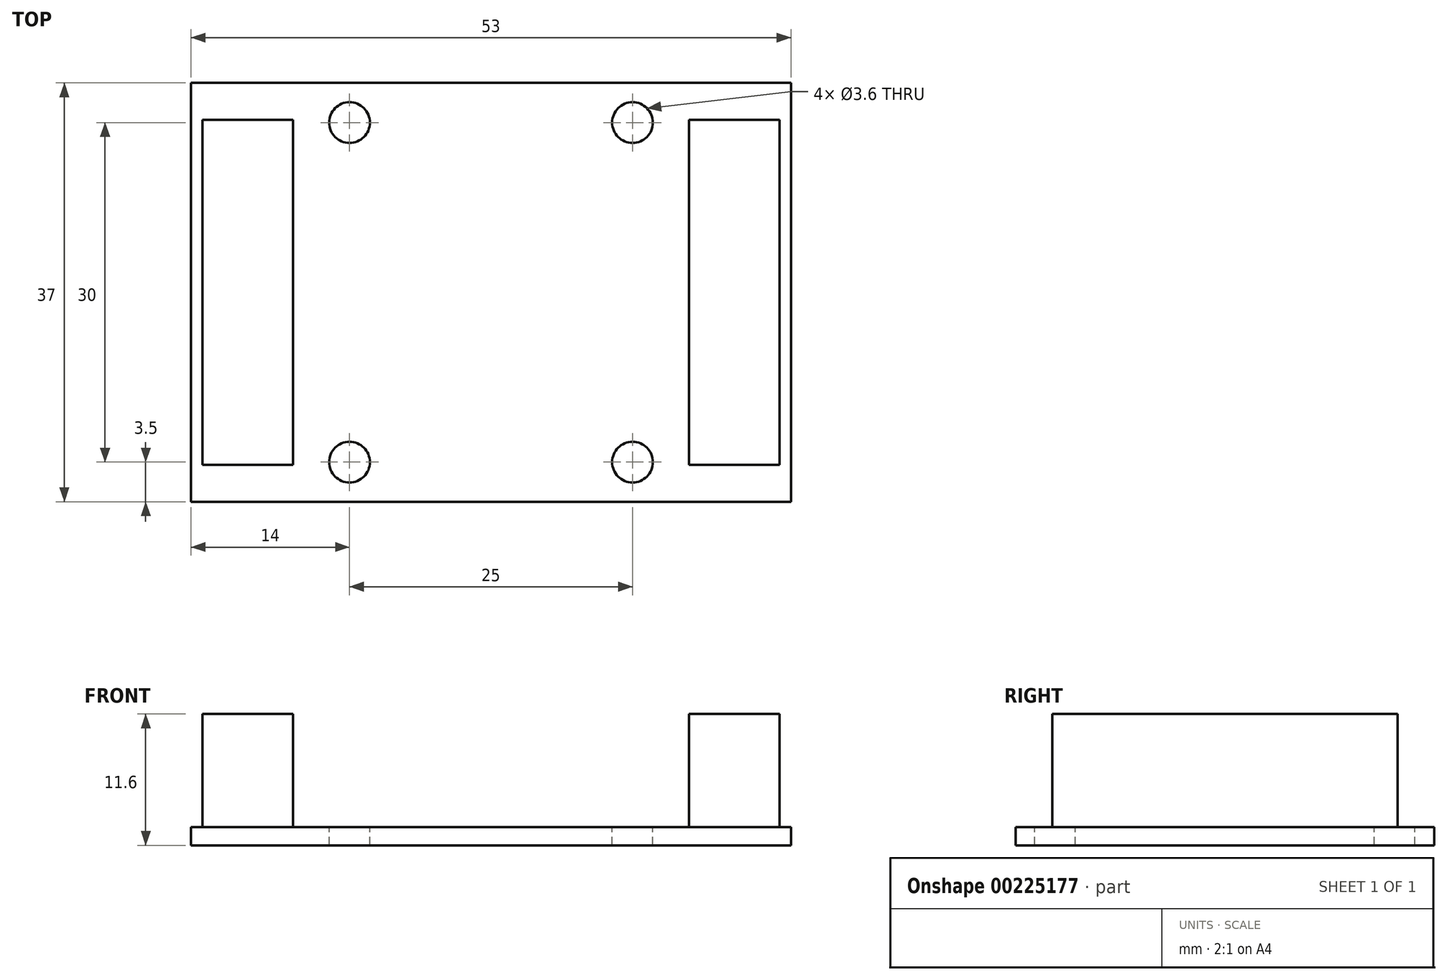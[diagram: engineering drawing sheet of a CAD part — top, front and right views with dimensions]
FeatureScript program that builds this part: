
annotation { "Feature Type Name" : "Feature", "Feature Type Description" : "" }
export const myFeature = defineFeature(function(context is Context, id is Id, definition is map)
    precondition{}
    {
        {
            var Q0;
            Q0=qCreatedBy(makeId("Top.planeOp"),FACE);
            var sketch = newSketch(context, id + "F0", { "sketchPlane" : qUnion([Q0])});
            skLineSegment(sketch, "E0.bottom", {"start": v(26.5, -18.5) * mm, "end": v(-26.5, -18.5) * mm});
            skLineSegment(sketch, "E0.top", {"start": v(26.5, 18.5) * mm, "end": v(-26.5, 18.5) * mm});
            skLineSegment(sketch, "E0.left", {"start": v(26.5, -18.5) * mm, "end": v(26.5, 18.5) * mm});
            skLineSegment(sketch, "E0.right", {"start": v(-26.5, -18.5) * mm, "end": v(-26.5, 18.5) * mm});
            skPoint(sketch, "E0.middle", {"position": v(0, 0) * mm});
            skSolve(sketch);
        }
        {
            var Q0;
            Q0=makeQuery(id+"F0.imprint","IMPRINT",FACE,{"disambiguationData":[TD([[makeQuery(id+"F0.imprint","IMPRINT",EDGE,{"derivedFrom":sQuery(id+"F0.wireOp",EDGE,"E0.bottom")}),-1.0]])]});
            extrude(context, id + "F1", {"entities" : qUnion([Q0]), "depth" : 1.6 * mm});
        }
        {
            var Q0;
            Q0=makeQuery(id+"F1.opExtrude","CAP_FACE",FACE,{"disambiguationData":[OSD([sQuery(id+"F0.wireOp",EDGE,"E0.bottom"),sQuery(id+"F0.wireOp",EDGE,"E0.top"),sQuery(id+"F0.wireOp",EDGE,"E0.left"),sQuery(id+"F0.wireOp",EDGE,"E0.right")])],"isStart":false});
            var sketch = newSketch(context, id + "F2", { "sketchPlane" : qUnion([Q0])});
            skLineSegment(sketch, "E1.bottom", {"start": v(-25.5, 15.25) * mm, "end": v(-17.5, 15.25) * mm});
            skLineSegment(sketch, "E1.top", {"start": v(-25.5, -15.25) * mm, "end": v(-17.5, -15.25) * mm});
            skLineSegment(sketch, "E1.left", {"start": v(-25.5, 15.25) * mm, "end": v(-25.5, -15.25) * mm});
            skLineSegment(sketch, "E1.right", {"start": v(-17.5, 15.25) * mm, "end": v(-17.5, -15.25) * mm});
            skLineSegment(sketch, "E2.bottom", {"start": v(17.5, 15.25) * mm, "end": v(25.5, 15.25) * mm});
            skLineSegment(sketch, "E2.top", {"start": v(17.5, -15.25) * mm, "end": v(25.5, -15.25) * mm});
            skLineSegment(sketch, "E2.left", {"start": v(17.5, 15.25) * mm, "end": v(17.5, -15.25) * mm});
            skLineSegment(sketch, "E2.right", {"start": v(25.5, 15.25) * mm, "end": v(25.5, -15.25) * mm});
            skSolve(sketch);
        }
        {
            var Q0;
            Q0=makeQuery(id+"F2.imprint","IMPRINT",FACE,{"disambiguationData":[TD([[makeQuery(id+"F2.imprint","IMPRINT",EDGE,{"derivedFrom":sQuery(id+"F2.wireOp",EDGE,"E2.bottom")}),-1.0]])]});
            var Q1;
            Q1=makeQuery(id+"F2.imprint","IMPRINT",FACE,{"disambiguationData":[TD([[makeQuery(id+"F2.imprint","IMPRINT",EDGE,{"derivedFrom":sQuery(id+"F2.wireOp",EDGE,"E1.bottom")}),-1.0]])]});
            extrude(context, id + "F3", {"entities" : qUnion([Q0, Q1]), "operationType" : NewBodyOperationType.ADD, "depth" : 10 * mm});
        }
        {
            var Q0;
            Q0=makeQuery(id+"F1.opExtrude","CAP_FACE",FACE,{"disambiguationData":[OSD([sQuery(id+"F0.wireOp",EDGE,"E0.bottom"),sQuery(id+"F0.wireOp",EDGE,"E0.top"),sQuery(id+"F0.wireOp",EDGE,"E0.left"),sQuery(id+"F0.wireOp",EDGE,"E0.right")])],"isStart":false});
            var sketch = newSketch(context, id + "F4", { "sketchPlane" : qUnion([Q0])});
            skCircle(sketch, "E3", {"center": v(12.5, -15) * mm, "radius": 1.8 * mm});
            skCircle(sketch, "E4.0.1.0", {"center": v(12.5, 15) * mm, "radius": 1.8 * mm});
            skCircle(sketch, "E4.1.0.0", {"center": v(-12.5, -15) * mm, "radius": 1.8 * mm});
            skCircle(sketch, "E4.1.1.0", {"center": v(-12.5, 15) * mm, "radius": 1.8 * mm});
            skLineSegment(sketch, "E4.direction1", {"start": v(12.5, -15) * mm, "end": v(-12.5, -15) * mm, "construction": true});
            skLineSegment(sketch, "E4.direction2", {"start": v(12.5, -15) * mm, "end": v(12.5, 15) * mm, "construction": true});
            skSolve(sketch);
        }
        {
            var Q0;
            Q0=makeQuery(id+"F4.imprint","IMPRINT",FACE,{"disambiguationData":[TD([[makeQuery(id+"F4.imprint","IMPRINT",EDGE,{"derivedFrom":sQuery(id+"F4.wireOp",EDGE,"E3")}),1.0]])]});
            var Q1;
            Q1=makeQuery(id+"F4.imprint","IMPRINT",FACE,{"disambiguationData":[TD([[makeQuery(id+"F4.imprint","IMPRINT",EDGE,{"derivedFrom":sQuery(id+"F4.wireOp",EDGE,"E4.0.1.0")}),1.0]])]});
            var Q2;
            Q2=makeQuery(id+"F4.imprint","IMPRINT",FACE,{"disambiguationData":[TD([[makeQuery(id+"F4.imprint","IMPRINT",EDGE,{"derivedFrom":sQuery(id+"F4.wireOp",EDGE,"E4.1.1.0")}),1.0]])]});
            var Q3;
            Q3=makeQuery(id+"F4.imprint","IMPRINT",FACE,{"disambiguationData":[TD([[makeQuery(id+"F4.imprint","IMPRINT",EDGE,{"derivedFrom":sQuery(id+"F4.wireOp",EDGE,"E4.1.0.0")}),1.0]])]});
            var Q4;
            Q4=sQuery(id+"F4.wireOp",EDGE,"E3");
            var Q5;
            Q5=sQuery(id+"F4.wireOp",EDGE,"E4.0.1.0");
            var Q6;
            Q6=sQuery(id+"F4.wireOp",EDGE,"E4.1.1.0");
            var Q7;
            Q7=sQuery(id+"F4.wireOp",EDGE,"E4.1.0.0");
            extrude(context, id + "F5", {"entities" : qUnion([Q0, Q1, Q2, Q3]), "operationType" : NewBodyOperationType.REMOVE, "surfaceEntities" : qUnion([Q4, Q5, Q6, Q7]), "endBound" : BoundingType.UP_TO_NEXT, "oppositeDirection" : true, "depth" : 25 * mm});
        }
    });
